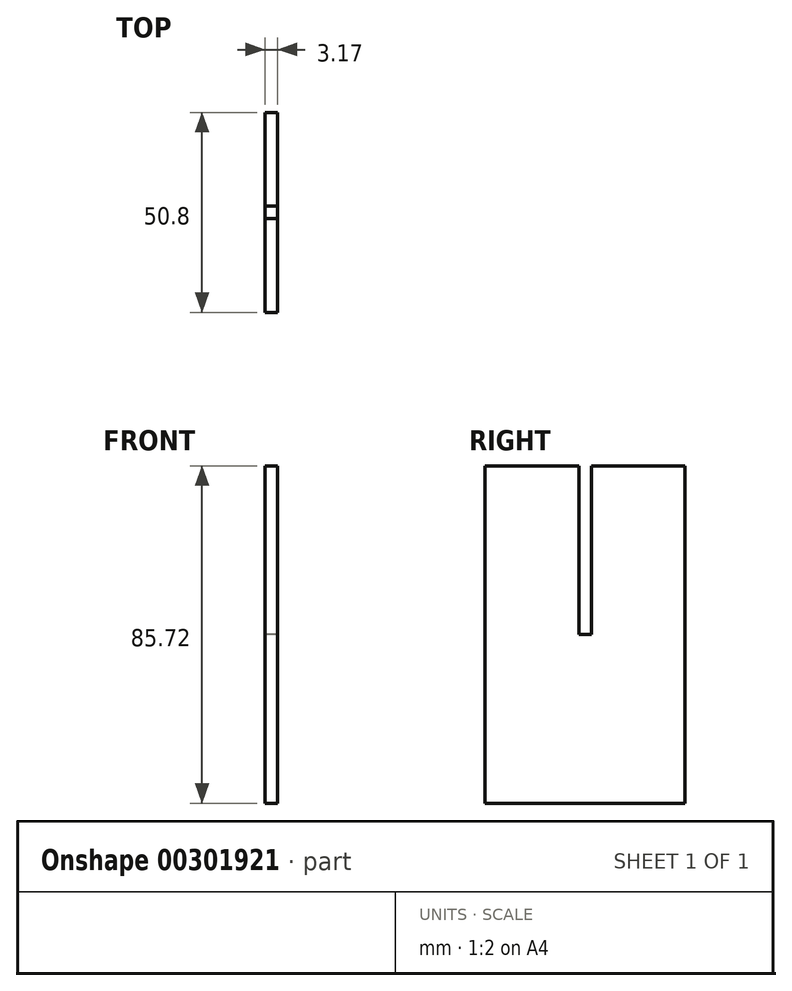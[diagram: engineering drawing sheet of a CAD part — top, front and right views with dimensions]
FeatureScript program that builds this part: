
annotation { "Feature Type Name" : "Feature", "Feature Type Description" : "" }
export const myFeature = defineFeature(function(context is Context, id is Id, definition is map)
    precondition{}
    {
        {
            var Q0;
            Q0=qCreatedBy(makeId("Right.planeOp"),FACE);
            var sketch = newSketch(context, id + "F0", { "sketchPlane" : qUnion([Q0])});
            skLineSegment(sketch, "E0.bottom", {"start": v(25.4, -42.86) * mm, "end": v(-25.4, -42.86) * mm});
            skLineSegment(sketch, "E0.top", {"start": v(25.4, 42.86) * mm, "end": v(-25.4, 42.86) * mm});
            skLineSegment(sketch, "E0.left", {"start": v(25.4, -42.86) * mm, "end": v(25.4, 42.86) * mm});
            skLineSegment(sketch, "E0.right", {"start": v(-25.4, -42.86) * mm, "end": v(-25.4, 42.86) * mm});
            skPoint(sketch, "E0.middle", {"position": v(0, 0) * mm});
            skLineSegment(sketch, "E1.bottom", {"start": v(-1.59, 42.86) * mm, "end": v(1.59, 42.86) * mm});
            skLineSegment(sketch, "E1.top", {"start": v(-1.59, 0) * mm, "end": v(1.59, 0) * mm});
            skLineSegment(sketch, "E1.left", {"start": v(-1.59, 42.86) * mm, "end": v(-1.59, 0) * mm});
            skLineSegment(sketch, "E1.right", {"start": v(1.59, 42.86) * mm, "end": v(1.59, 0) * mm});
            skSolve(sketch);
        }
        {
            var Q0;
            Q0=makeQuery(id+"F0.imprint","IMPRINT",FACE,{"disambiguationData":[TD([[makeQuery(id+"F0.imprint","IMPRINT",EDGE,{"derivedFrom":sQuery(id+"F0.wireOp",EDGE,"E0.bottom")}),-1.0]])]});
            extrude(context, id + "F1", {"entities" : qUnion([Q0]), "depth" : 3.17 * mm});
        }
    });
